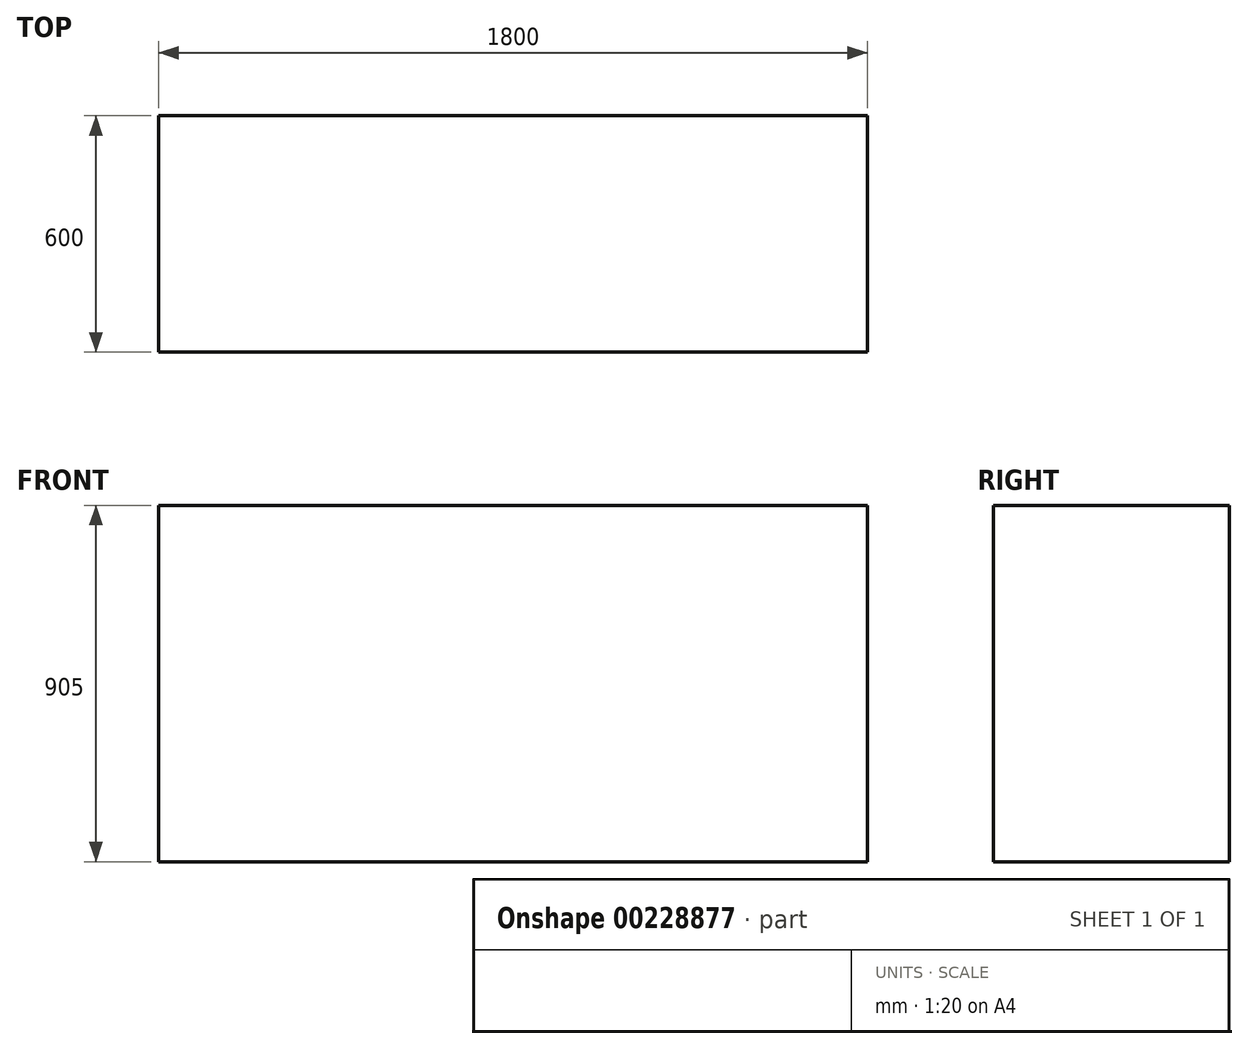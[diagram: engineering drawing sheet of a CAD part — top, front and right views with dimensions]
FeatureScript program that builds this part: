
annotation { "Feature Type Name" : "Feature", "Feature Type Description" : "" }
export const myFeature = defineFeature(function(context is Context, id is Id, definition is map)
    precondition{}
    {
        {
            var Q0;
            Q0=qCreatedBy(makeId("Top.planeOp"),FACE);
            var sketch = newSketch(context, id + "F0", { "sketchPlane" : qUnion([Q0])});
            skLineSegment(sketch, "E0.bottom", {"start": v(0, 0) * mm, "end": v(1800, 0) * mm});
            skLineSegment(sketch, "E0.top", {"start": v(0, -600) * mm, "end": v(1800, -600) * mm});
            skLineSegment(sketch, "E0.left", {"start": v(0, 0) * mm, "end": v(0, -600) * mm});
            skLineSegment(sketch, "E0.right", {"start": v(1800, 0) * mm, "end": v(1800, -600) * mm});
            skSolve(sketch);
        }
        {
            var Q0;
            Q0 = qSketchRegion(id + "F0", true);
            extrude(context, id + "F1", {"entities" : qUnion([Q0]), "depth" : 905 * mm});
        }
    });
